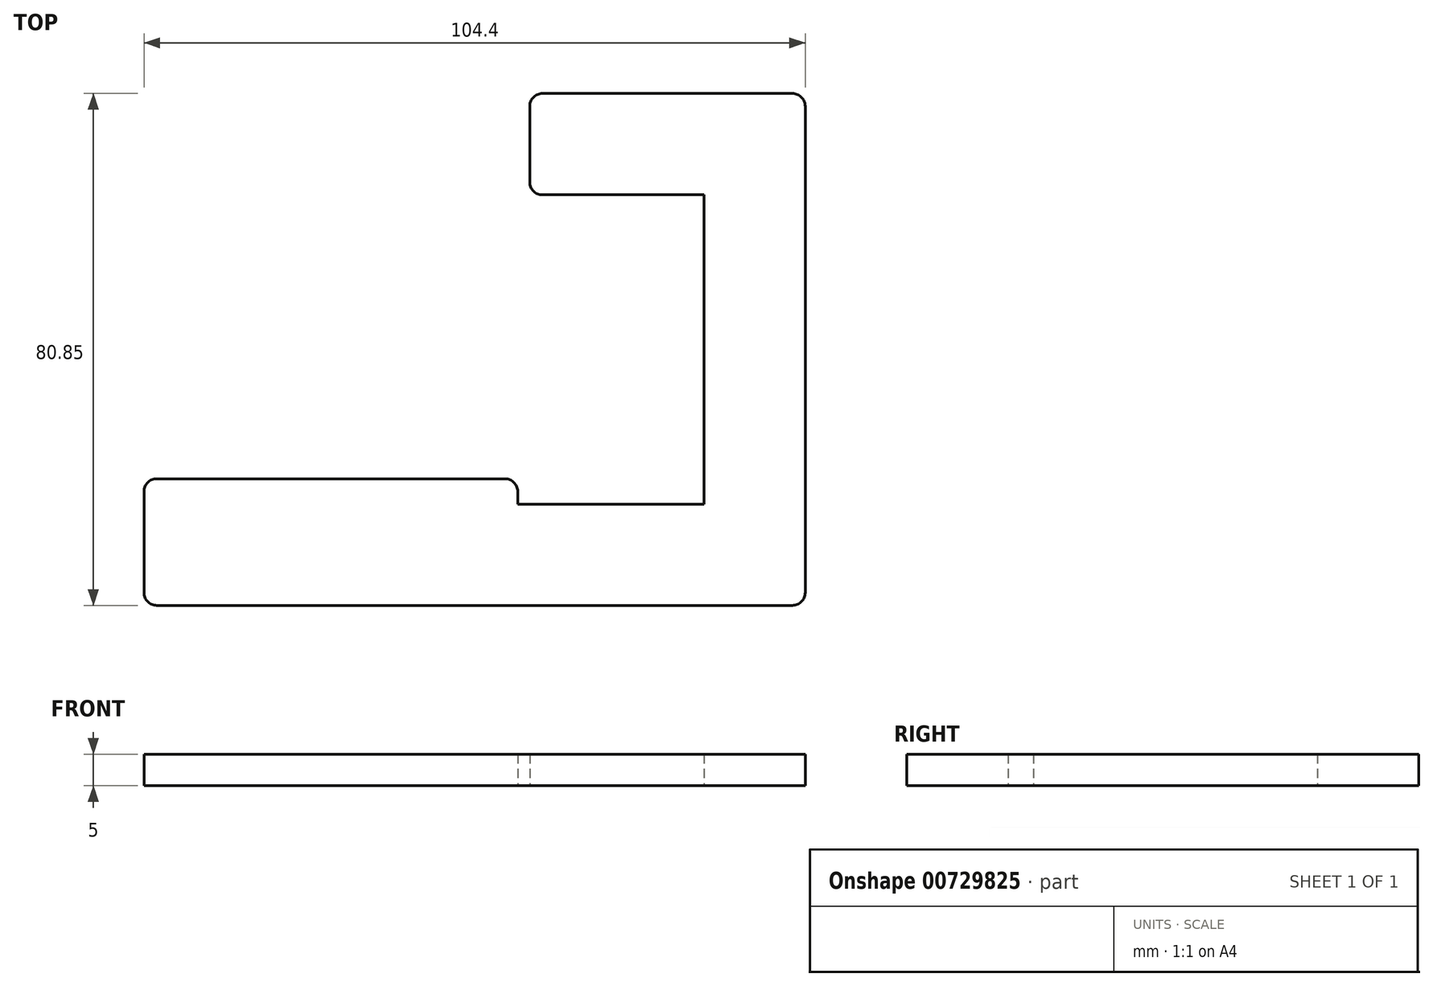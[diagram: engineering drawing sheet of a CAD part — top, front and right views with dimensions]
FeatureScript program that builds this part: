
annotation { "Feature Type Name" : "Feature", "Feature Type Description" : "" }
export const myFeature = defineFeature(function(context is Context, id is Id, definition is map)
    precondition{}
    {
        {
            var Q0;
            Q0=qCreatedBy(makeId("Top.planeOp"),FACE);
            var sketch = newSketch(context, id + "F0", { "sketchPlane" : qUnion([Q0])});
            skLineSegment(sketch, "E0", {"start": v(-65.16, 28.92) * mm, "end": v(-39.66, 28.92) * mm});
            skLineSegment(sketch, "E1", {"start": v(-39.66, 28.92) * mm, "end": v(-39.66, -19.93) * mm});
            skLineSegment(sketch, "E2", {"start": v(-39.66, -19.93) * mm, "end": v(-69.06, -19.93) * mm});
            skLineSegment(sketch, "E3", {"start": v(-69.06, -19.93) * mm, "end": v(-69.06, -17.93) * mm});
            skLineSegment(sketch, "E4", {"start": v(-71.06, -15.93) * mm, "end": v(-88.06, -15.93) * mm});
            skLineSegment(sketch, "E5", {"start": v(-88.06, -15.93) * mm, "end": v(-126.06, -15.93) * mm});
            skLineSegment(sketch, "E6", {"start": v(-128.06, -17.93) * mm, "end": v(-128.06, -33.93) * mm});
            skLineSegment(sketch, "E7", {"start": v(-39.66, -35.93) * mm, "end": v(-126.06, -35.93) * mm});
            skLineSegment(sketch, "E8", {"start": v(-23.66, -19.93) * mm, "end": v(-23.66, -33.93) * mm});
            skLineSegment(sketch, "E9", {"start": v(-25.66, -35.93) * mm, "end": v(-39.66, -35.93) * mm});
            skLineSegment(sketch, "E10", {"start": v(-23.66, 28.92) * mm, "end": v(-23.66, -19.93) * mm});
            skLineSegment(sketch, "E11", {"start": v(-67.16, 30.92) * mm, "end": v(-67.16, 42.92) * mm});
            skLineSegment(sketch, "E12", {"start": v(-65.16, 44.92) * mm, "end": v(-25.66, 44.92) * mm});
            skLineSegment(sketch, "E13", {"start": v(-23.66, 42.92) * mm, "end": v(-23.66, 28.92) * mm});
            skPoint(sketch, "E14.visualSharp", {"position": v(-69.06, -15.93) * mm});
            skArc(sketch, "E14.filletArc", {"start": v(-69.06, -17.93) * mm, "mid": v(-69.65, -16.52) * mm, "end": v(-71.06, -15.93) * mm});
            skPoint(sketch, "E15.visualSharp", {"position": v(-128.06, -15.93) * mm});
            skArc(sketch, "E15.filletArc", {"start": v(-126.06, -15.93) * mm, "mid": v(-127.48, -16.52) * mm, "end": v(-128.06, -17.93) * mm});
            skPoint(sketch, "E16.visualSharp", {"position": v(-128.06, -35.93) * mm});
            skArc(sketch, "E16.filletArc", {"start": v(-128.06, -33.93) * mm, "mid": v(-127.48, -35.35) * mm, "end": v(-126.06, -35.93) * mm});
            skPoint(sketch, "E17.visualSharp", {"position": v(-23.66, -35.93) * mm});
            skArc(sketch, "E17.filletArc", {"start": v(-25.66, -35.93) * mm, "mid": v(-24.25, -35.35) * mm, "end": v(-23.66, -33.93) * mm});
            skPoint(sketch, "E18.visualSharp", {"position": v(-23.66, 44.92) * mm});
            skArc(sketch, "E18.filletArc", {"start": v(-23.66, 42.92) * mm, "mid": v(-24.25, 44.33) * mm, "end": v(-25.66, 44.92) * mm});
            skPoint(sketch, "E19.visualSharp", {"position": v(-67.16, 44.92) * mm});
            skArc(sketch, "E19.filletArc", {"start": v(-65.16, 44.92) * mm, "mid": v(-66.58, 44.33) * mm, "end": v(-67.16, 42.92) * mm});
            skPoint(sketch, "E20.visualSharp", {"position": v(-67.16, 28.92) * mm});
            skArc(sketch, "E20.filletArc", {"start": v(-67.16, 30.92) * mm, "mid": v(-66.58, 29.5) * mm, "end": v(-65.16, 28.92) * mm});
            skSolve(sketch);
        }
        {
            var Q0;
            Q0 = qSketchRegion(id + "F0", true);
            extrude(context, id + "F1", {"entities" : qUnion([Q0]), "depth" : 5 * mm, "offsetDistance" : 25 * mm});
        }
    });
